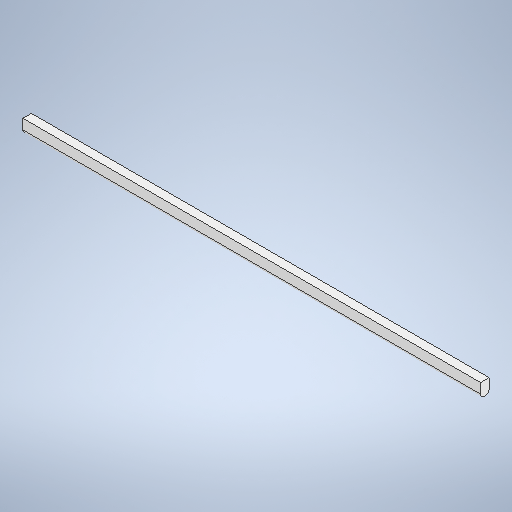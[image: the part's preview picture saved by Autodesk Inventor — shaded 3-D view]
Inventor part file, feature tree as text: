
AUTODESK INVENTOR PART (.ipt)
format: ipt  version: 2025 (Build 290162000, 162)  size: 260,608 bytes
history: native  units: in
note: dims shown in document units (in); Inventor stores cm internally (conversion verified against a paired STEP export)
features: fillet x2, other x2, extrude x1, sketch x1
ambient origin geometry x8: Origin, YZ Plane, XZ Plane, XY Plane, X Axis, Y Axis, Z Axis, Center Point
bodies: Solid1 (feature_tree)
feature tree (6):
  extrude  "Extrusion1"  Depth=46.6142in
  fillet  "Fillet1"  Radius=0.8661in
  fillet  "Fillet2"  Radius=0.3937in
  sketch  "Sketch1"  dims[d0=1.4173in d1=46.6142in d2=0.8661in d3=0.0in d4=0.3937in d5=0.3937in]
  other  "Finish1"
  other  "Finish2"
